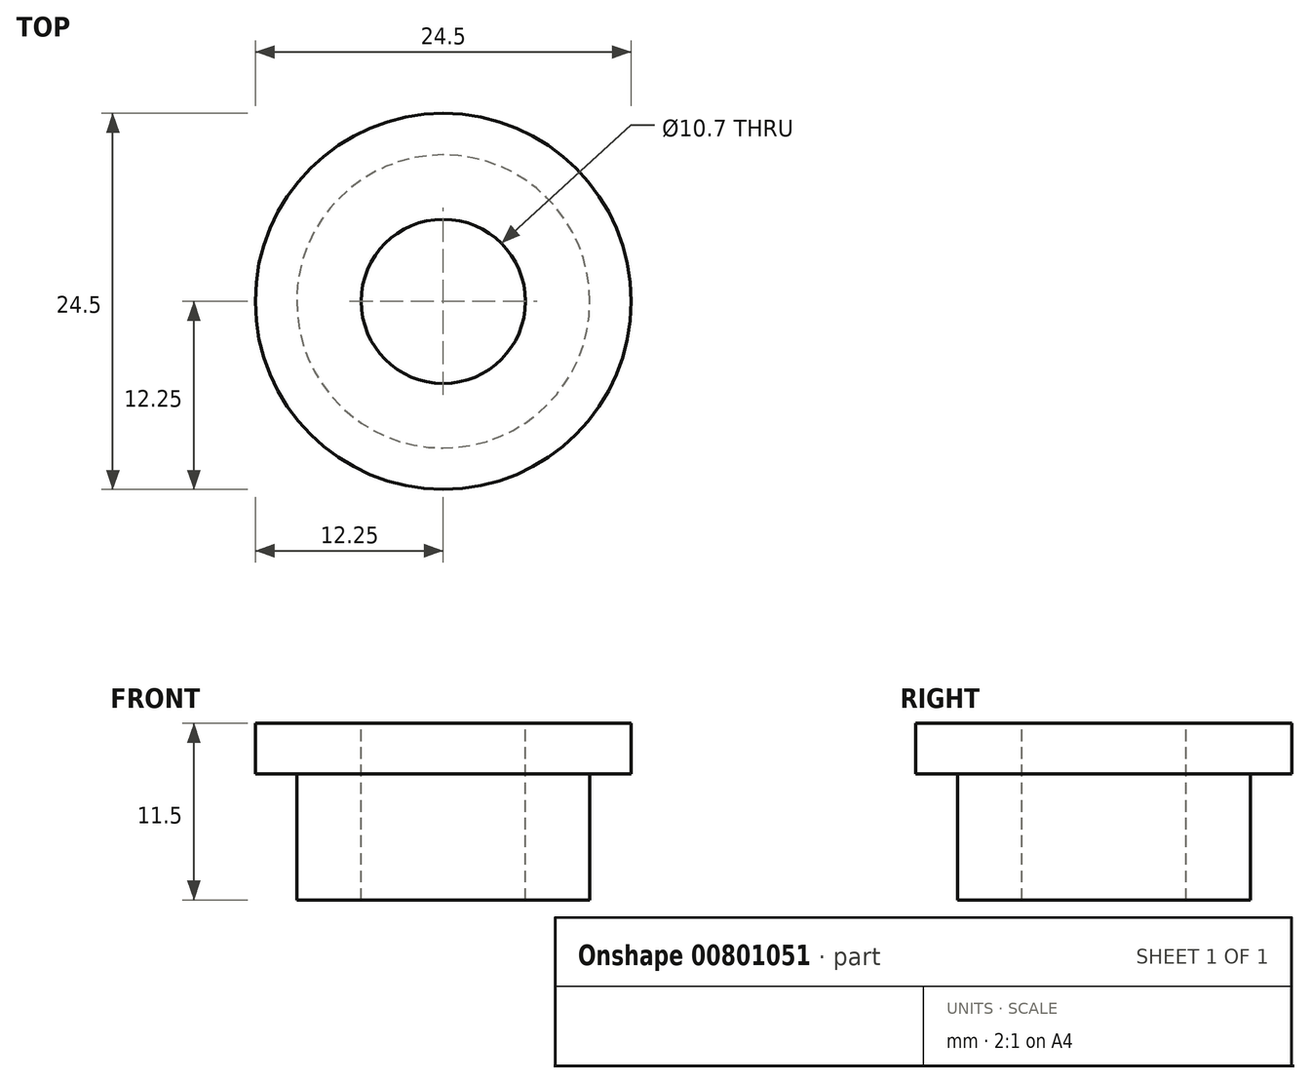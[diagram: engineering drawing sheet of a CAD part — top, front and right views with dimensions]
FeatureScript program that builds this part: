
annotation { "Feature Type Name" : "Feature", "Feature Type Description" : "" }
export const myFeature = defineFeature(function(context is Context, id is Id, definition is map)
    precondition{}
    {
        {
            var Q0;
            Q0=qCreatedBy(makeId("Front.planeOp"),FACE);
            var sketch = newSketch(context, id + "F0", { "sketchPlane" : qUnion([Q0])});
            skLineSegment(sketch, "E0", {"start": v(0, 0) * mm, "end": v(0, -11.5) * mm});
            skLineSegment(sketch, "E1", {"start": v(0, -11.5) * mm, "end": v(9.55, -11.5) * mm});
            skLineSegment(sketch, "E2", {"start": v(9.55, -11.5) * mm, "end": v(9.55, -3.3) * mm});
            skLineSegment(sketch, "E3", {"start": v(9.55, -3.3) * mm, "end": v(12.25, -3.3) * mm});
            skLineSegment(sketch, "E4", {"start": v(12.25, -3.3) * mm, "end": v(12.25, 0) * mm});
            skLineSegment(sketch, "E5", {"start": v(12.25, 0) * mm, "end": v(0, 0) * mm});
            skLineSegment(sketch, "E6", {"start": v(5.35, 0) * mm, "end": v(5.35, -11.5) * mm});
            skSolve(sketch);
        }
        {
            var Q0;
            {var subQ1=sQuery(id+"F0.wireOp",EDGE,"E2");Q0=makeQuery(id+"F0.imprint","IMPRINT",FACE,{"disambiguationData":[TD([[makeQuery(id+"F0.imprint","IMPRINT",EDGE,{"derivedFrom":subQ1}),1.0]])]});}
            var Q1;
            Q1=sQuery(id+"F0.wireOp",EDGE,"E0");
            revolve(context, id + "F1", {"surfaceOperationType" : NewSurfaceOperationType.NEW, "entities" : qUnion([Q0]), "axis" : qUnion([Q1]), "revolveType" : RevolveType.FULL});
        }
    });
